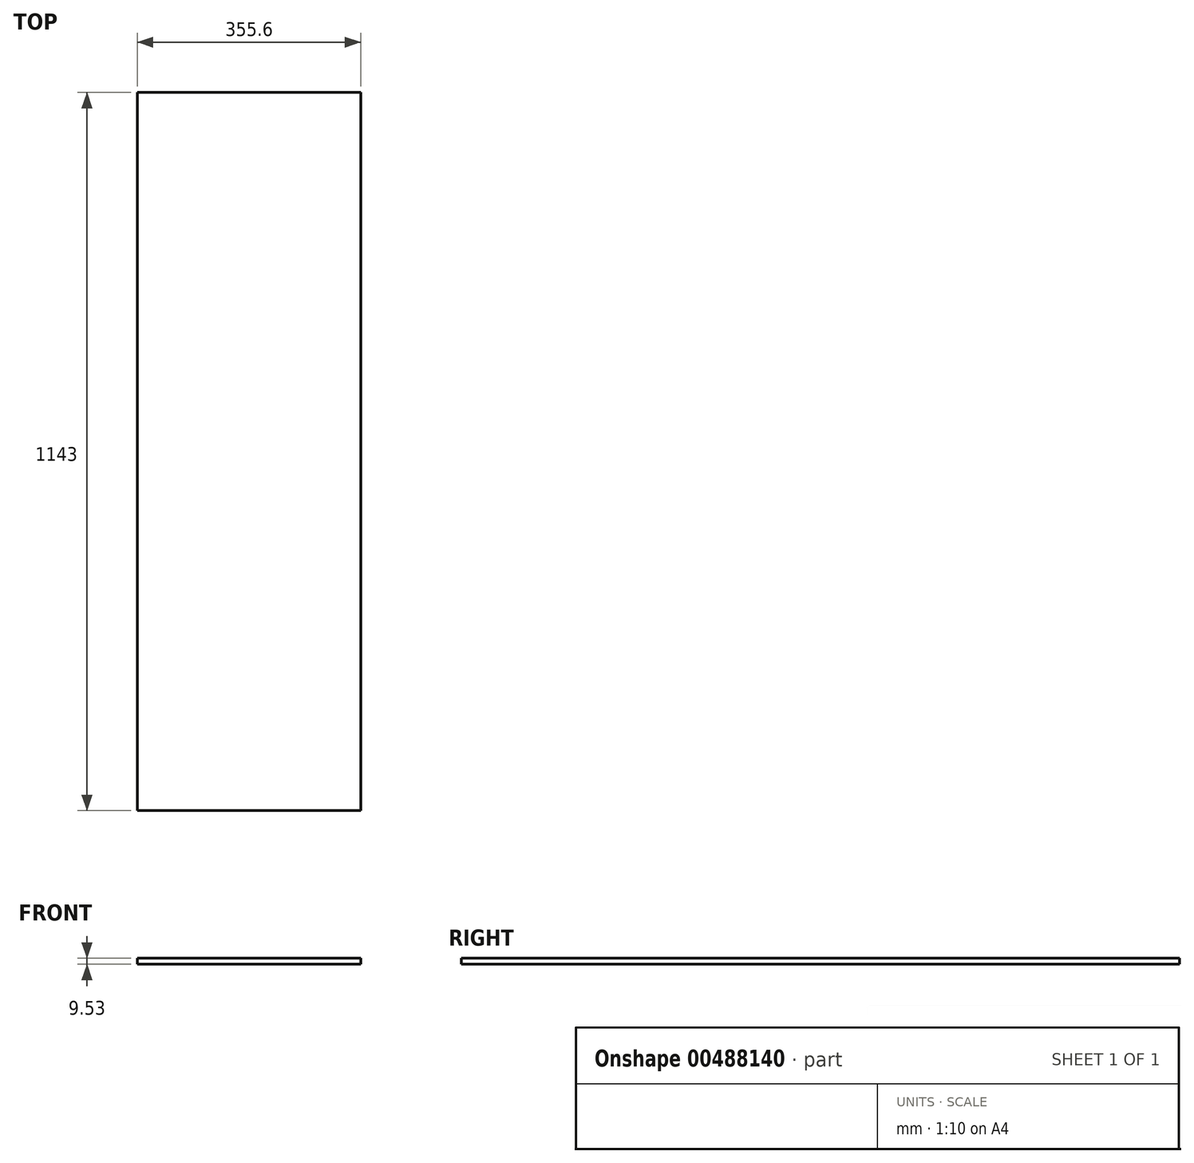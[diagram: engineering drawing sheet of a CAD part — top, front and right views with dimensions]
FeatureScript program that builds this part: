
annotation { "Feature Type Name" : "Feature", "Feature Type Description" : "" }
export const myFeature = defineFeature(function(context is Context, id is Id, definition is map)
    precondition{}
    {
        {
            var Q0;
            Q0=qCreatedBy(makeId("Front.planeOp"),FACE);
            var sketch = newSketch(context, id + "F0", { "sketchPlane" : qUnion([Q0])});
            skLineSegment(sketch, "E0", {"start": v(0, 0) * mm, "end": v(0, 9.52) * mm});
            skLineSegment(sketch, "E1", {"start": v(0, 9.52) * mm, "end": v(355.6, 9.52) * mm});
            skLineSegment(sketch, "E2", {"start": v(355.6, 9.52) * mm, "end": v(355.6, 0) * mm});
            skLineSegment(sketch, "E3", {"start": v(355.6, 0) * mm, "end": v(0, 0) * mm});
            skSolve(sketch);
        }
        {
            var Q0;
            Q0=makeQuery(id+"F0.imprint","IMPRINT",FACE,{"disambiguationData":[TD([[makeQuery(id+"F0.imprint","IMPRINT",EDGE,{"derivedFrom":sQuery(id+"F0.wireOp",EDGE,"E0")}),-1.0]])]});
            extrude(context, id + "F1", {"entities" : qUnion([Q0]), "depth" : 1143 * mm, "offsetDistance" : 25.4 * mm});
        }
    });
